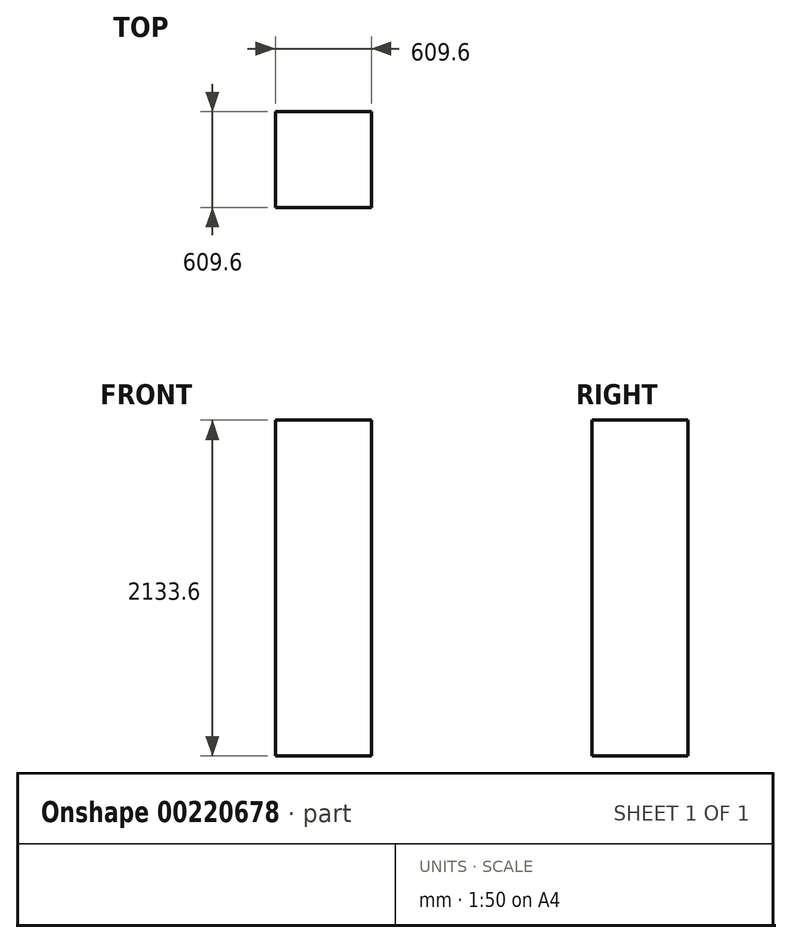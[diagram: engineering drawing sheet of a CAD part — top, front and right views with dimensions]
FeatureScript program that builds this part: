
annotation { "Feature Type Name" : "Feature", "Feature Type Description" : "" }
export const myFeature = defineFeature(function(context is Context, id is Id, definition is map)
    precondition{}
    {
        {
            var Q0;
            Q0=qCreatedBy(makeId("Top.planeOp"),FACE);
            var sketch = newSketch(context, id + "F0", { "sketchPlane" : qUnion([Q0])});
            skLineSegment(sketch, "E0.bottom", {"start": v(304.8, -288.06) * mm, "end": v(-304.8, -288.06) * mm});
            skLineSegment(sketch, "E0.top", {"start": v(304.8, 321.54) * mm, "end": v(-304.8, 321.54) * mm});
            skLineSegment(sketch, "E0.left", {"start": v(304.8, -288.06) * mm, "end": v(304.8, 321.54) * mm});
            skLineSegment(sketch, "E0.right", {"start": v(-304.8, -288.06) * mm, "end": v(-304.8, 321.54) * mm});
            skPoint(sketch, "E0.middle", {"position": v(0, 16.74) * mm});
            skSolve(sketch);
        }
        {
            var Q0;
            Q0 = qSketchRegion(id + "F0", true);
            extrude(context, id + "F1", {"entities" : qUnion([Q0]), "depth" : 2133.6 * mm});
        }
    });
